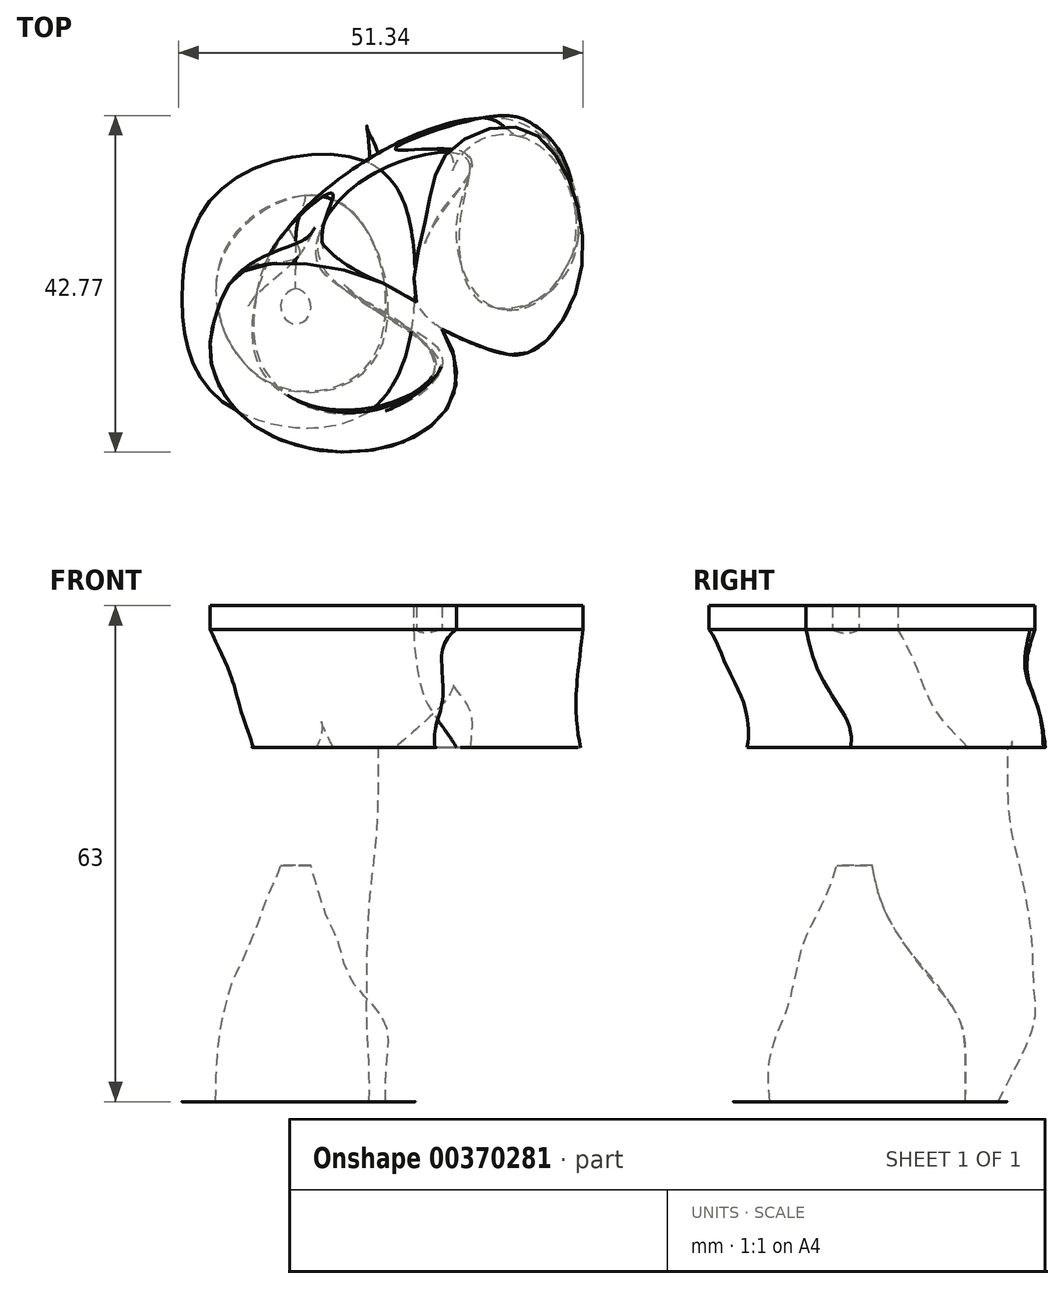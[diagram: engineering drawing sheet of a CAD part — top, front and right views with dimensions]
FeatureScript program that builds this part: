
annotation { "Feature Type Name" : "Feature", "Feature Type Description" : "" }
export const myFeature = defineFeature(function(context is Context, id is Id, definition is map)
    precondition{}
    {
        {
            var Q0;
            Q0=qCreatedBy(makeId("Top.planeOp"),FACE);
            cPlane(context, id + "F0", {"entities" : qUnion([Q0]), "cplaneType" : CPlaneType.OFFSET, "offset" : 5 * mm, "width" : 152.4 * mm, "height" : 152.4 * mm});
        }
        {
            var Q0;
            Q0=qCreatedBy(id+"F0.planeOp",FACE);
            var sketch = newSketch(context, id + "F1", { "sketchPlane" : qUnion([Q0])});
            skFitSpline(sketch, "E0", {"points": [v(0, 17.84) * mm, v(-18.32, 14.95) * mm, v(-23.78, 0) * mm, v(-18.32, -12.7) * mm, v(0, -13.66) * mm, v(5.79, 5.3) * mm, v(0, 17.84) * mm]});
            skSolve(sketch);
        }
        {
            var Q0;
            Q0=qCreatedBy(id+"F0.planeOp",FACE);
            var sketch = newSketch(context, id + "F2", { "sketchPlane" : qUnion([Q0])});
            skFitSpline(sketch, "E1", {"points": [v(-8.27, 13.68) * mm, v(-19.1, 4.63) * mm, v(-13.19, -9.74) * mm, v(0, -7.58) * mm, v(0, 8.76) * mm, v(-8.27, 13.68) * mm]});
            skSolve(sketch);
        }
        {
            var Q0;
            Q0=qCreatedBy(id+"F0.planeOp",FACE);
            cPlane(context, id + "F3", {"entities" : qUnion([Q0]), "cplaneType" : CPlaneType.OFFSET, "offset" : 5 * mm, "width" : 152.4 * mm, "height" : 152.4 * mm});
        }
        {
            var Q0;
            Q0=qCreatedBy(id+"F3.planeOp",FACE);
            var sketch = newSketch(context, id + "F4", { "sketchPlane" : qUnion([Q0])});
            skFitSpline(sketch, "E2", {"points": [v(-18.96, -12.05) * mm, v(-24.1, 0) * mm, v(-18, 15.59) * mm, v(0, 20.4) * mm, v(7.07, 18.16) * mm, v(5.46, 5.3) * mm, v(5.79, -4.02) * mm, v(0, -13.98) * mm, v(-18.96, -12.05) * mm]});
            skSolve(sketch);
        }
        {
            var Q0;
            Q0=qCreatedBy(id+"F3.planeOp",FACE);
            var sketch = newSketch(context, id + "F5", { "sketchPlane" : qUnion([Q0])});
            skFitSpline(sketch, "E3", {"points": [v(-8.66, 13.68) * mm, v(-18.9, 4.82) * mm, v(-13.58, -9.55) * mm, v(0, -7.97) * mm, v(0, 8.76) * mm, v(-8.66, 13.68) * mm]});
            skSolve(sketch);
        }
        {
            var Q0;
            Q0=qCreatedBy(id+"F3.planeOp",FACE);
            cPlane(context, id + "F6", {"entities" : qUnion([Q0]), "cplaneType" : CPlaneType.OFFSET, "offset" : 5 * mm, "width" : 152.4 * mm, "height" : 152.4 * mm});
        }
        {
            var Q0;
            Q0=qCreatedBy(id+"F6.planeOp",FACE);
            var sketch = newSketch(context, id + "F7", { "sketchPlane" : qUnion([Q0])});
            skFitSpline(sketch, "E4", {"points": [v(-18.32, -11.73) * mm, v(-22.18, 0) * mm, v(-15.1, 16.23) * mm, v(2.57, 22.66) * mm, v(9.96, 20.09) * mm, v(3.86, 6.91) * mm, v(3.86, -4.02) * mm, v(0, -13.98) * mm, v(-18.32, -11.73) * mm]});
            skSolve(sketch);
        }
        {
            var Q0;
            Q0=qCreatedBy(id+"F6.planeOp",FACE);
            var sketch = newSketch(context, id + "F8", { "sketchPlane" : qUnion([Q0])});
            skFitSpline(sketch, "E5", {"points": [v(-9.25, 12.9) * mm, v(-18.7, 0) * mm, v(-13, -8.56) * mm, v(0, -6.99) * mm, v(0, 7.58) * mm, v(-9.25, 12.9) * mm]});
            skSolve(sketch);
        }
        {
            var Q0;
            Q0=qCreatedBy(id+"F6.planeOp",FACE);
            cPlane(context, id + "F9", {"entities" : qUnion([Q0]), "cplaneType" : CPlaneType.OFFSET, "offset" : 5 * mm, "width" : 152.4 * mm, "height" : 152.4 * mm});
        }
        {
            var Q0;
            Q0=qCreatedBy(id+"F9.planeOp",FACE);
            var sketch = newSketch(context, id + "F10", { "sketchPlane" : qUnion([Q0])});
            skFitSpline(sketch, "E6", {"points": [v(-20.57, 0) * mm, v(-12.54, 15.91) * mm, v(4.5, 23.3) * mm, v(13.82, 22.02) * mm, v(11.57, 17.2) * mm, v(5.46, 12.7) * mm, v(0, 5.3) * mm, v(2.57, -6.91) * mm, v(0, -14.62) * mm, v(-16.4, -11.41) * mm, v(-20.57, 0) * mm]});
            skSolve(sketch);
        }
        {
            var Q0;
            Q0=qCreatedBy(id+"F9.planeOp",FACE);
            var sketch = newSketch(context, id + "F11", { "sketchPlane" : qUnion([Q0])});
            skFitSpline(sketch, "E7", {"points": [v(-12.2, 9.74) * mm, v(-17.32, 2.07) * mm, v(-13.58, -6.99) * mm, v(-2.95, -5.6) * mm, v(-5.12, 6.8) * mm, v(-12.2, 9.74) * mm]});
            skSolve(sketch);
        }
        {
            var Q0;
            Q0=qCreatedBy(id+"F9.planeOp",FACE);
            cPlane(context, id + "F12", {"entities" : qUnion([Q0]), "cplaneType" : CPlaneType.OFFSET, "offset" : 5 * mm, "width" : 152.4 * mm, "height" : 152.4 * mm});
        }
        {
            var Q0;
            Q0=qCreatedBy(id+"F12.planeOp",FACE);
            var sketch = newSketch(context, id + "F13", { "sketchPlane" : qUnion([Q0])});
            skFitSpline(sketch, "E8", {"points": [v(-14.52, -9.94) * mm, v(-18.07, 0) * mm, v(-10.74, 15.39) * mm, v(3.93, 23.17) * mm, v(15.7, 20.94) * mm, v(15.04, 16.5) * mm, v(8.15, 14.5) * mm, v(0, 10.72) * mm, v(-2.07, 5.17) * mm, v(1.7, -3.28) * mm, v(0, -13.5) * mm, v(-14.52, -9.94) * mm]});
            skSolve(sketch);
        }
        {
            var Q0;
            Q0=qCreatedBy(id+"F12.planeOp",FACE);
            var sketch = newSketch(context, id + "F14", { "sketchPlane" : qUnion([Q0])});
            skFitSpline(sketch, "E9", {"points": [v(-9.45, 6) * mm, v(-14.57, 2.26) * mm, v(-13, -5.6) * mm, v(-4.72, -5.41) * mm, v(-5.31, 2.66) * mm, v(-9.45, 6) * mm]});
            skSolve(sketch);
        }
        {
            var Q0;
            Q0=qCreatedBy(id+"F12.planeOp",FACE);
            cPlane(context, id + "F15", {"entities" : qUnion([Q0]), "cplaneType" : CPlaneType.OFFSET, "offset" : 5 * mm, "width" : 152.4 * mm, "height" : 152.4 * mm});
        }
        {
            var Q0;
            Q0=qCreatedBy(id+"F15.planeOp",FACE);
            var sketch = newSketch(context, id + "F16", { "sketchPlane" : qUnion([Q0])});
            skFitSpline(sketch, "E10", {"points": [v(-12.74, -8.6) * mm, v(-16.07, 0) * mm, v(-9.18, 14.94) * mm, v(3.04, 22.5) * mm, v(16.37, 21.39) * mm, v(18.81, 15.83) * mm, v(7.26, 14.5) * mm, v(-2.07, 11.61) * mm, v(-4.07, 4.28) * mm, v(0, -4.17) * mm, v(2.37, -11.05) * mm, v(-2.74, -13.72) * mm, v(-12.74, -8.6) * mm]});
            skSolve(sketch);
        }
        {
            var Q0;
            Q0=qCreatedBy(id+"F15.planeOp",FACE);
            var sketch = newSketch(context, id + "F17", { "sketchPlane" : qUnion([Q0])});
            skFitSpline(sketch, "E11", {"points": [v(-11.02, 2.85) * mm, v(-13.19, 0) * mm, v(-12, -4.03) * mm, v(-6.5, -3.05) * mm, v(-7.28, 2.26) * mm, v(-11.02, 2.85) * mm]});
            skSolve(sketch);
        }
        {
            var Q0;
            Q0=qCreatedBy(id+"F15.planeOp",FACE);
            cPlane(context, id + "F18", {"entities" : qUnion([Q0]), "cplaneType" : CPlaneType.OFFSET, "offset" : 5 * mm, "width" : 152.4 * mm, "height" : 152.4 * mm});
        }
        {
            var Q0;
            Q0=qCreatedBy(id+"F18.planeOp",FACE);
            var sketch = newSketch(context, id + "F19", { "sketchPlane" : qUnion([Q0])});
            skFitSpline(sketch, "E12", {"points": [v(-10.96, -7.28) * mm, v(-13.63, 0) * mm, v(-7.63, 13.83) * mm, v(5.48, 22.72) * mm, v(16.15, 21.17) * mm, v(21.04, 11.39) * mm, v(12.37, 14.06) * mm, v(2.15, 14.28) * mm, v(-5.18, 8.28) * mm, v(-3.4, 0) * mm, v(2.15, -9.05) * mm, v(0, -13.05) * mm, v(-10.96, -7.28) * mm]});
            skSolve(sketch);
        }
        {
            var Q0;
            Q0=qCreatedBy(id+"F18.planeOp",FACE);
            var sketch = newSketch(context, id + "F20", { "sketchPlane" : qUnion([Q0])});
            skFitSpline(sketch, "E13", {"points": [v(-9.25, 1.87) * mm, v(-11.22, 0) * mm, v(-10.04, -2.46) * mm, v(-8.07, -2.07) * mm, v(-7.48, 0) * mm, v(-9.25, 1.87) * mm]});
            skSolve(sketch);
        }
        {
            var Q0;
            Q0=qCreatedBy(id+"F18.planeOp",FACE);
            cPlane(context, id + "F21", {"entities" : qUnion([Q0]), "cplaneType" : CPlaneType.OFFSET, "offset" : 5 * mm, "width" : 152.4 * mm, "height" : 152.4 * mm});
        }
        {
            var Q0;
            Q0=qCreatedBy(id+"F21.planeOp",FACE);
            var sketch = newSketch(context, id + "F22", { "sketchPlane" : qUnion([Q0])});
            skFitSpline(sketch, "E14", {"points": [v(-10.63, -7.77) * mm, v(-10.63, 0) * mm, v(-6.89, 13.88) * mm, v(5.12, 20.96) * mm, v(16.73, 22.14) * mm, v(22.64, 12.5) * mm, v(21.65, 7.77) * mm, v(14.76, 11.9) * mm, v(11.8, 15.45) * mm, v(1.57, 15.65) * mm, v(-5.12, 6) * mm, v(-1.97, -1.67) * mm, v(1.38, -8.56) * mm, v(0, -12.5) * mm, v(-10.63, -7.77) * mm]});
            skSolve(sketch);
        }
        {
            var Q0;
            Q0=qCreatedBy(id+"F21.planeOp",FACE);
            cPlane(context, id + "F23", {"entities" : qUnion([Q0]), "cplaneType" : CPlaneType.OFFSET, "offset" : 5 * mm, "width" : 152.4 * mm, "height" : 152.4 * mm});
        }
        {
            var Q0;
            Q0=qCreatedBy(id+"F23.planeOp",FACE);
            var sketch = newSketch(context, id + "F24", { "sketchPlane" : qUnion([Q0])});
            skFitSpline(sketch, "E15", {"points": [v(-4.13, -13.68) * mm, v(-12.6, -7.77) * mm, v(-12.8, 0) * mm, v(-10.43, 7.58) * mm, v(-3.54, 16.44) * mm, v(11.42, 22.34) * mm, v(17.71, 22.14) * mm, v(23.03, 17.81) * mm, v(24.8, 8.37) * mm, v(18.3, 2.46) * mm, v(12.8, 9.35) * mm, v(11.42, 18.2) * mm, v(4.72, 18) * mm, v(-2.56, 11.9) * mm, v(-5.12, 6.2) * mm, v(0, -2.26) * mm, v(4.33, -11.32) * mm, v(-4.13, -13.68) * mm]});
            skSolve(sketch);
        }
        {
            var Q0;
            Q0=qCreatedBy(id+"F23.planeOp",FACE);
            cPlane(context, id + "F25", {"entities" : qUnion([Q0]), "cplaneType" : CPlaneType.OFFSET, "offset" : 5 * mm, "width" : 152.4 * mm, "height" : 152.4 * mm});
        }
        {
            var Q0;
            Q0=qCreatedBy(id+"F25.planeOp",FACE);
            var sketch = newSketch(context, id + "F26", { "sketchPlane" : qUnion([Q0])});
            skFitSpline(sketch, "E16", {"points": [v(-11.02, 8.56) * mm, v(-14.57, 0) * mm, v(-13, -9.55) * mm, v(0, -13.29) * mm, v(8.46, -7.18) * mm, v(-5.31, 3.84) * mm, v(-4.33, 12.5) * mm, v(5.7, 18.6) * mm, v(12.4, 18.4) * mm, v(11.61, 11.12) * mm, v(14.57, 0) * mm, v(25.4, 4.43) * mm, v(21.85, 21.36) * mm, v(7.68, 22.14) * mm, v(-5.31, 14.66) * mm, v(-11.02, 8.56) * mm]});
            skSolve(sketch);
        }
        {
            var Q0;
            Q0=qCreatedBy(id+"F25.planeOp",FACE);
            var sketch = newSketch(context, id + "F27", { "sketchPlane" : qUnion([Q0])});
            skFitSpline(sketch, "E17", {"points": [v(-4.62, 13.97) * mm, v(-11.1, 8.63) * mm, v(-14.5, 0) * mm, v(-13.48, -8.12) * mm, v(-3.15, -14.02) * mm, v(8.37, -8.12) * mm, v(0, 0) * mm, v(-6.76, 6.58) * mm, v(-4.62, 13.97) * mm]});
            skSolve(sketch);
        }
        {
            var Q0;
            Q0=qCreatedBy(id+"F25.planeOp",FACE);
            var sketch = newSketch(context, id + "F28", { "sketchPlane" : qUnion([Q0])});
            skFitSpline(sketch, "E18", {"points": [v(3.31, 19.57) * mm, v(15.16, 23.72) * mm, v(22.04, 21.55) * mm, v(26.77, 11.71) * mm, v(25.2, 5.02) * mm, v(21.06, 0) * mm, v(14.96, 0) * mm, v(11.22, 10.92) * mm, v(12.13, 19.12) * mm, v(3.31, 19.57) * mm]});
            skSolve(sketch);
        }
        {
            var Q0;
            Q0=qCreatedBy(id+"F25.planeOp",FACE);
            cPlane(context, id + "F29", {"entities" : qUnion([Q0]), "cplaneType" : CPlaneType.OFFSET, "offset" : 5 * mm, "width" : 152.4 * mm, "height" : 152.4 * mm});
        }
        {
            var Q0;
            Q0=qCreatedBy(id+"F29.planeOp",FACE);
            var sketch = newSketch(context, id + "F30", { "sketchPlane" : qUnion([Q0])});
            skFitSpline(sketch, "E19", {"points": [v(-8.86, 6.2) * mm, v(-15.16, 0) * mm, v(-14.96, -8.76) * mm, v(0, -14.07) * mm, v(9.05, -7.18) * mm, v(-3.94, 3.25) * mm, v(-6.7, 9.74) * mm, v(-8.86, 6.2) * mm]});
            skSolve(sketch);
        }
        {
            var Q0;
            Q0=qCreatedBy(id+"F29.planeOp",FACE);
            var sketch = newSketch(context, id + "F31", { "sketchPlane" : qUnion([Q0])});
            skFitSpline(sketch, "E20", {"points": [v(8.86, 20.57) * mm, v(12.6, 17.22) * mm, v(8.66, 10.92) * mm, v(10.63, 0) * mm, v(22.83, 0) * mm, v(25, 17.62) * mm, v(16.73, 22.93) * mm, v(8.86, 20.57) * mm]});
            skSolve(sketch);
        }
        {
            var Q0;
            Q0=qCreatedBy(id+"F29.planeOp",FACE);
            cPlane(context, id + "F32", {"entities" : qUnion([Q0]), "cplaneType" : CPlaneType.OFFSET, "offset" : 5 * mm, "width" : 152.4 * mm, "height" : 152.4 * mm});
        }
        {
            var Q0;
            Q0=qCreatedBy(id+"F32.planeOp",FACE);
            var sketch = newSketch(context, id + "F33", { "sketchPlane" : qUnion([Q0])});
            skFitSpline(sketch, "E21", {"points": [v(-5.9, 7.18) * mm, v(-14.76, 4.43) * mm, v(-17.91, -5.8) * mm, v(-16.53, -11.9) * mm, v(-6.3, -16.44) * mm, v(9.25, -7.38) * mm, v(0, 0) * mm, v(-5.9, 7.18) * mm]});
            skSolve(sketch);
        }
        {
            var Q0;
            Q0=qCreatedBy(id+"F32.planeOp",FACE);
            var sketch = newSketch(context, id + "F34", { "sketchPlane" : qUnion([Q0])});
            skFitSpline(sketch, "E22", {"points": [v(13.19, 20.37) * mm, v(9.05, 13.09) * mm, v(6.3, 5.41) * mm, v(8.27, -1.87) * mm, v(20.67, -4.43) * mm, v(26.57, 7.18) * mm, v(21.45, 20.17) * mm, v(13.19, 20.37) * mm]});
            skSolve(sketch);
        }
        {
            var Q0;
            Q0=qCreatedBy(id+"F32.planeOp",FACE);
            cPlane(context, id + "F35", {"entities" : qUnion([Q0]), "cplaneType" : CPlaneType.OFFSET, "offset" : 5 * mm, "width" : 152.4 * mm, "height" : 152.4 * mm});
        }
        {
            var Q0;
            Q0=qCreatedBy(id+"F35.planeOp",FACE);
            var sketch = newSketch(context, id + "F36", { "sketchPlane" : qUnion([Q0])});
            skFitSpline(sketch, "E23", {"points": [v(-14.78, 4.58) * mm, v(-18.98, 0) * mm, v(-20.1, -7.2) * mm, v(-14.52, -15.6) * mm, v(0, -18.69) * mm, v(10.48, -12.22) * mm, v(6.26, 0) * mm, v(-14.78, 4.58) * mm]});
            skSolve(sketch);
        }
        {
            var Q0;
            Q0=qCreatedBy(id+"F35.planeOp",FACE);
            var sketch = newSketch(context, id + "F37", { "sketchPlane" : qUnion([Q0])});
            skFitSpline(sketch, "E24", {"points": [v(13.58, -5.22) * mm, v(6.1, 0) * mm, v(7.28, 11.12) * mm, v(9.84, 19) * mm, v(19.1, 22.34) * mm, v(25.78, 14.66) * mm, v(26.37, 1.87) * mm, v(20.27, -6.2) * mm, v(13.58, -5.22) * mm]});
            skSolve(sketch);
        }
        {
            var Q0;
            Q0 = qSketchRegion(id + "F1", true);
            var Q1;
            Q1 = qSketchRegion(id + "F4", true);
            var Q2;
            Q2 = qSketchRegion(id + "F7", true);
            var Q3;
            Q3 = qSketchRegion(id + "F10", true);
            var Q4;
            Q4 = qSketchRegion(id + "F13", true);
            var Q5;
            Q5 = qSketchRegion(id + "F16", true);
            var Q6;
            Q6 = qSketchRegion(id + "F19", true);
            var Q7;
            Q7 = qSketchRegion(id + "F22", true);
            var Q8;
            Q8 = qSketchRegion(id + "F24", true);
            var Q9;
            Q9 = qSketchRegion(id + "F26", true);
            loft(context, id + "F38", {"sheetProfilesArray" : [{ "sheetProfileEntities" : qUnion([Q0]) }, { "sheetProfileEntities" : qUnion([Q1]) }, { "sheetProfileEntities" : qUnion([Q2]) }, { "sheetProfileEntities" : qUnion([Q3]) }, { "sheetProfileEntities" : qUnion([Q4]) }, { "sheetProfileEntities" : qUnion([Q5]) }, { "sheetProfileEntities" : qUnion([Q6]) }, { "sheetProfileEntities" : qUnion([Q7]) }, { "sheetProfileEntities" : qUnion([Q8]) }, { "sheetProfileEntities" : qUnion([Q9]) }]});
        }
        {
            var Q1;
            Q1 = qSketchRegion(id + "F27", true);
            var Q2;
            Q2 = qSketchRegion(id + "F30", true);
            var Q3;
            Q3 = qSketchRegion(id + "F33", true);
            var Q4;
            Q4 = qSketchRegion(id + "F36", true);
            loft(context, id + "F39", {"operationType" : NewBodyOperationType.ADD, "sheetProfilesArray" : [{ "sheetProfileEntities" : qUnion([Q1]) }, { "sheetProfileEntities" : qUnion([Q2]) }, { "sheetProfileEntities" : qUnion([Q3]) }, { "sheetProfileEntities" : qUnion([Q4]) }]});
        }
        {
            var Q1;
            Q1 = qSketchRegion(id + "F28", true);
            var Q2;
            Q2 = qSketchRegion(id + "F31", true);
            var Q3;
            Q3 = qSketchRegion(id + "F34", true);
            var Q4;
            Q4 = qSketchRegion(id + "F37", true);
            loft(context, id + "F40", {"operationType" : NewBodyOperationType.ADD, "sheetProfilesArray" : [{ "sheetProfileEntities" : qUnion([Q1]) }, { "sheetProfileEntities" : qUnion([Q2]) }, { "sheetProfileEntities" : qUnion([Q3]) }, { "sheetProfileEntities" : qUnion([Q4]) }]});
        }
        {
            var Q0;
            Q0=makeQuery(id+"F40.boolean.opBoolean","MERGE",FACE,{"derivedFrom":[makeQuery(id+"F39.opLoft","CAP_FACE",FACE,{"disambiguationData":[OSD([makeQuery(id+"F36.imprint","IMPRINT",FACE,{"disambiguationData":[TD([[makeQuery(id+"F36.imprint","IMPRINT",EDGE,{"derivedFrom":sQuery(id+"F36.wireOp",EDGE,"E23")}),1.0]])]})])],"isStart":true}),makeQuery(id+"F40.opLoft","CAP_FACE",FACE,{"disambiguationData":[OSD([makeQuery(id+"F37.imprint","IMPRINT",FACE,{"disambiguationData":[TD([[makeQuery(id+"F37.imprint","IMPRINT",EDGE,{"derivedFrom":sQuery(id+"F37.wireOp",EDGE,"E24")}),-1.0]])]})])],"isStart":true})]});
            extrude(context, id + "F41", {"entities" : qUnion([Q0]), "operationType" : NewBodyOperationType.ADD, "depth" : 3 * mm});
        }
        {
            var Q1;
            Q1 = qSketchRegion(id + "F2", true);
            var Q2;
            Q2 = qSketchRegion(id + "F5", true);
            var Q3;
            Q3 = qSketchRegion(id + "F8", true);
            var Q4;
            Q4 = qSketchRegion(id + "F11", true);
            var Q5;
            Q5 = qSketchRegion(id + "F14", true);
            var Q6;
            Q6 = qSketchRegion(id + "F17", true);
            var Q7;
            Q7 = qSketchRegion(id + "F20", true);
            loft(context, id + "F42", {"operationType" : NewBodyOperationType.REMOVE, "sheetProfilesArray" : [{ "sheetProfileEntities" : qUnion([Q1]) }, { "sheetProfileEntities" : qUnion([Q2]) }, { "sheetProfileEntities" : qUnion([Q3]) }, { "sheetProfileEntities" : qUnion([Q4]) }, { "sheetProfileEntities" : qUnion([Q5]) }, { "sheetProfileEntities" : qUnion([Q6]) }, { "sheetProfileEntities" : qUnion([Q7]) }]});
        }
    });
